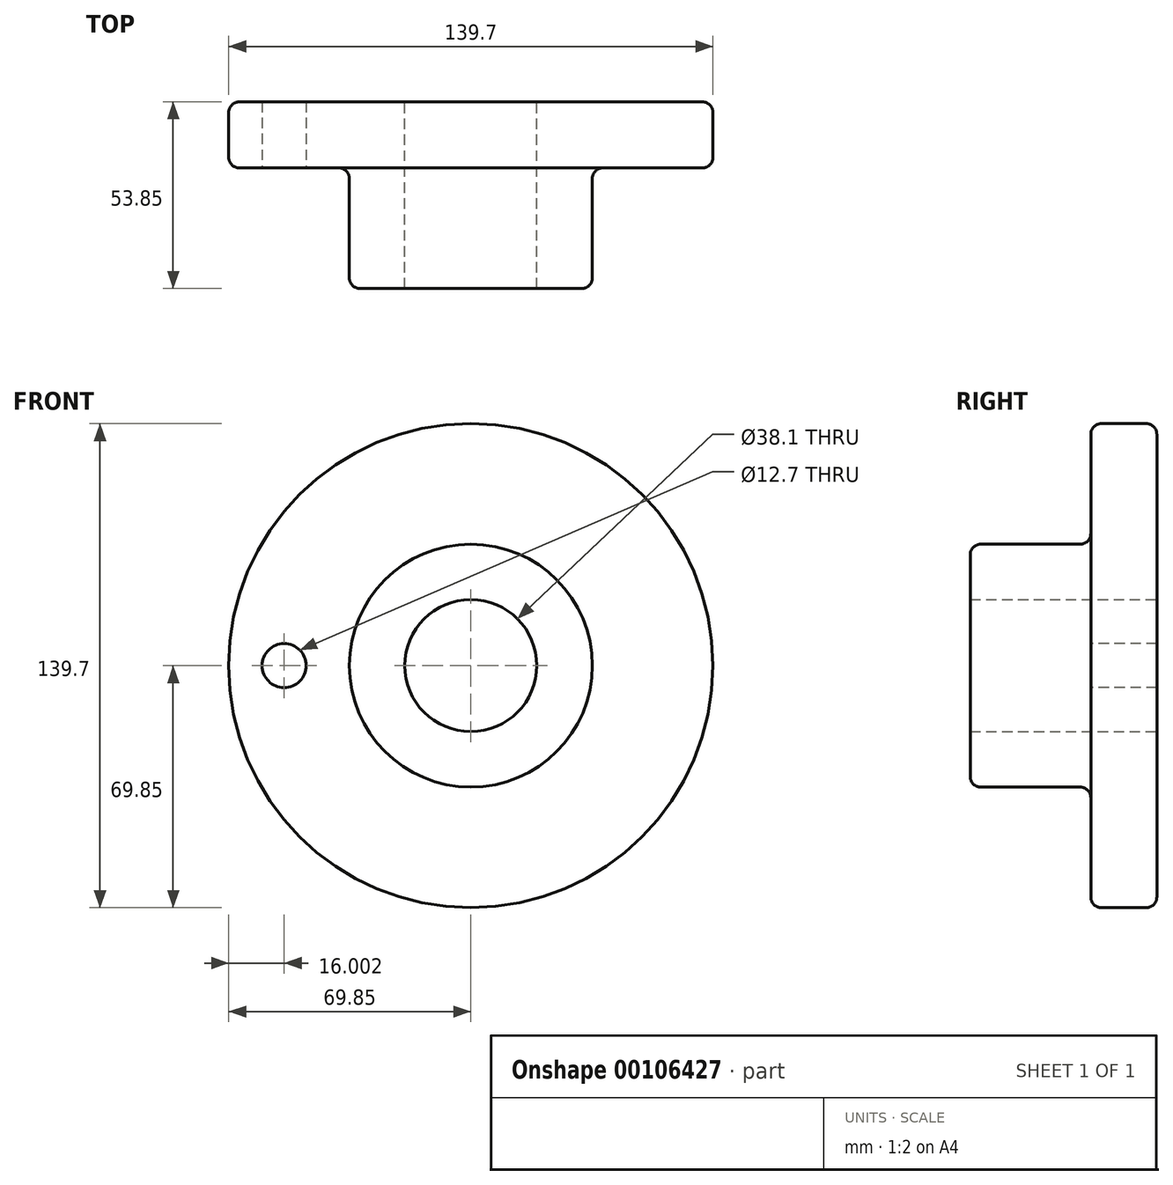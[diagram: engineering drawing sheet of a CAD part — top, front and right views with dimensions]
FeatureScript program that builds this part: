
annotation { "Feature Type Name" : "Feature", "Feature Type Description" : "" }
export const myFeature = defineFeature(function(context is Context, id is Id, definition is map)
    precondition{}
    {
        {
            var Q0;
            Q0=qCreatedBy(makeId("Right.planeOp"),FACE);
            var sketch = newSketch(context, id + "F0", { "sketchPlane" : qUnion([Q0])});
            skLineSegment(sketch, "E0.bottom", {"start": v(0, 0) * mm, "end": v(-53.85, 0) * mm});
            skLineSegment(sketch, "E0.top", {"start": v(0, 19.05) * mm, "end": v(-53.85, 19.05) * mm});
            skLineSegment(sketch, "E0.left", {"start": v(0, 0) * mm, "end": v(0, 19.05) * mm});
            skLineSegment(sketch, "E0.right", {"start": v(-53.85, 0) * mm, "end": v(-53.85, 19.05) * mm});
            skLineSegment(sketch, "E1", {"start": v(0, 19.05) * mm, "end": v(0, 69.85) * mm});
            skLineSegment(sketch, "E2", {"start": v(0, 69.85) * mm, "end": v(-19.05, 69.85) * mm});
            skLineSegment(sketch, "E3", {"start": v(-19.05, 69.85) * mm, "end": v(-19.05, 35.05) * mm});
            skLineSegment(sketch, "E4", {"start": v(-19.05, 35.05) * mm, "end": v(-53.85, 35.05) * mm});
            skLineSegment(sketch, "E5", {"start": v(-53.85, 35.05) * mm, "end": v(-53.85, 19.05) * mm});
            skSolve(sketch);
        }
        {
            var Q0;
            Q0=makeQuery(id+"F0.imprint","IMPRINT",FACE,{"disambiguationData":[TD([[makeQuery(id+"F0.imprint","IMPRINT",EDGE,{"derivedFrom":sQuery(id+"F0.wireOp",EDGE,"E0.top")}),-1.0]])]});
            var Q1;
            Q1=sQuery(id+"F0.wireOp",EDGE,"E0.bottom");
            revolve(context, id + "F1", {"entities" : qUnion([Q0]), "axis" : qUnion([Q1]), "revolveType" : RevolveType.ONE_DIRECTION, "angle" : 360 * degree});
        }
        {
            var Q0;
            Q0=makeQuery(id+"F1.opRevolve","SWEPT_FACE",FACE,{"disambiguationData":[OSD([sQuery(id+"F0.wireOp",EDGE,"E3")])]});
            var sketch = newSketch(context, id + "F2", { "sketchPlane" : qUnion([Q0])});
            skCircle(sketch, "E6", {"center": v(0, 0) * mm, "radius": 53.85 * mm});
            skCircle(sketch, "E7", {"center": v(-53.85, 0) * mm, "radius": 6.35 * mm});
            skSolve(sketch);
        }
        {
            var Q0;
            Q0=makeQuery(id+"F1.opRevolve","SWEPT_EDGE",EDGE,{"disambiguationData":[OSD([sQuery(id+"F0.wireOp",EDGE,"E2"),sQuery(id+"F0.wireOp",EDGE,"E3")])]});
            var Q1;
            Q1=makeQuery(id+"F1.opRevolve","SWEPT_EDGE",EDGE,{"disambiguationData":[OSD([sQuery(id+"F0.wireOp",EDGE,"E1"),sQuery(id+"F0.wireOp",EDGE,"E2")])]});
            var Q2;
            Q2=makeQuery(id+"F1.opRevolve","SWEPT_EDGE",EDGE,{"disambiguationData":[OSD([sQuery(id+"F0.wireOp",EDGE,"E3"),sQuery(id+"F0.wireOp",EDGE,"E4")])]});
            var Q3;
            Q3=makeQuery(id+"F1.opRevolve","SWEPT_EDGE",EDGE,{"disambiguationData":[OSD([sQuery(id+"F0.wireOp",EDGE,"E4"),sQuery(id+"F0.wireOp",EDGE,"E5")])]});
            fillet(context, id + "F3", {"entities" : qUnion([Q0, Q1, Q2, Q3]), "radius" : 3.05 * mm, "tangentPropagation" : true, "allowEdgeOverflow" : false});
        }
        {
            var Q0;
            {var subQ0=sQuery(id+"F2.wireOp",EDGE,"E7");var subQ1=sQuery(id+"F2.wireOp",EDGE,"E6");var subQ2=makeQuery(id+"F2.imprint","INTERSECT",VERTEX,{"disambiguationData":[OD(0.0)],"derivedFrom":[subQ1,subQ0]});Q0=makeQuery(id+"F2.imprint","IMPRINT",FACE,{"disambiguationData":[TD([[makeQuery(id+"F2.imprint","IMPRINT",EDGE,{"disambiguationData":[TD([[subQ2,1.0]])],"derivedFrom":subQ1}),1.0]])]});}
            var Q1;
            {var subQ0=sQuery(id+"F2.wireOp",EDGE,"E7");var subQ1=sQuery(id+"F2.wireOp",EDGE,"E6");var subQ2=makeQuery(id+"F2.imprint","INTERSECT",VERTEX,{"disambiguationData":[OD(0.0)],"derivedFrom":[subQ1,subQ0]});Q1=makeQuery(id+"F2.imprint","IMPRINT",FACE,{"disambiguationData":[TD([[makeQuery(id+"F2.imprint","IMPRINT",EDGE,{"disambiguationData":[TD([[subQ2,1.0]])],"derivedFrom":subQ1}),-1.0]])]});}
            extrude(context, id + "F4", {"entities" : qUnion([Q0, Q1]), "operationType" : NewBodyOperationType.REMOVE, "endBound" : BoundingType.THROUGH_ALL, "oppositeDirection" : true, "depth" : 25.4 * mm});
        }
    });
